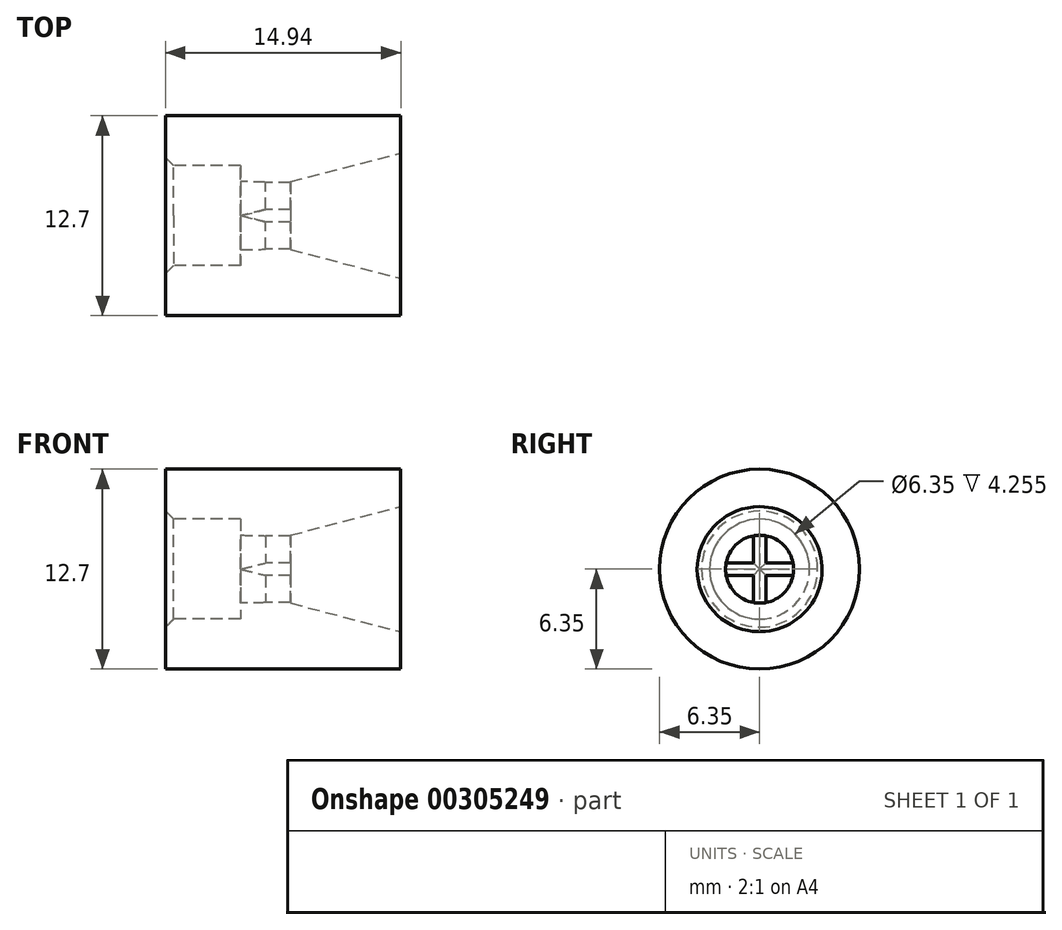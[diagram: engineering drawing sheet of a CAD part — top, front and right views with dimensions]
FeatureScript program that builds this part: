
annotation { "Feature Type Name" : "Feature", "Feature Type Description" : "" }
export const myFeature = defineFeature(function(context is Context, id is Id, definition is map)
    precondition{}
    {
        {
            var Q0;
            Q0=qCreatedBy(makeId("Top.planeOp"),FACE);
            var sketch = newSketch(context, id + "F0", { "sketchPlane" : qUnion([Q0])});
            skLineSegment(sketch, "E0", {"start": v(0, 0) * mm, "end": v(43.8, 0) * mm, "construction": true});
            skLineSegment(sketch, "E1", {"start": v(0, 6.35) * mm, "end": v(0, 3.17) * mm});
            skLineSegment(sketch, "E2", {"start": v(0, 3.17) * mm, "end": v(4.76, 3.17) * mm});
            skLineSegment(sketch, "E3", {"start": v(4.76, 3.17) * mm, "end": v(4.76, 2.16) * mm});
            skLineSegment(sketch, "E4", {"start": v(4.76, 2.16) * mm, "end": v(7.94, 2.16) * mm});
            skLineSegment(sketch, "E5", {"start": v(7.94, 2.16) * mm, "end": v(14.94, 3.97) * mm});
            skLineSegment(sketch, "E6", {"start": v(14.94, 3.97) * mm, "end": v(14.94, 6.35) * mm});
            skLineSegment(sketch, "E7", {"start": v(14.94, 6.35) * mm, "end": v(0, 6.35) * mm});
            skSolve(sketch);
        }
        {
            var Q0;
            Q0 = qSketchRegion(id + "F0", true);
            var Q1;
            Q1=sQuery(id+"F0.wireOp",EDGE,"E0");
            revolve(context, id + "F1", {"entities" : qUnion([Q0]), "axis" : qUnion([Q1]), "revolveType" : RevolveType.FULL});
        }
        {
            var Q0;
            Q0=makeQuery(id+"F1.opRevolve","SWEPT_EDGE",EDGE,{"disambiguationData":[OSD([sQuery(id+"F0.wireOp",EDGE,"E1"),sQuery(id+"F0.wireOp",EDGE,"E2")])]});
            chamfer(context, id + "F2", {"entities" : qUnion([Q0]), "width" : 0.5 * mm, "tangentPropagation" : true});
        }
        {
            var Q0;
            Q0=qCreatedBy(makeId("Top.planeOp"),FACE);
            var sketch = newSketch(context, id + "F3", { "sketchPlane" : qUnion([Q0])});
            skLineSegment(sketch, "E8", {"start": v(4.76, 2.16) * mm, "end": v(7.94, 2.16) * mm});
            skLineSegment(sketch, "E9", {"start": v(7.94, -2.16) * mm, "end": v(4.76, -2.16) * mm});
            skLineSegment(sketch, "E10.0.0", {"start": v(4.76, -3.17) * mm, "end": v(4.76, 3.17) * mm});
            skLineSegment(sketch, "E11.0", {"start": v(7.94, -2.16) * mm, "end": v(7.94, 2.16) * mm});
            skLineSegment(sketch, "E12", {"start": v(4.76, 0) * mm, "end": v(6.35, 0.4) * mm});
            skLineSegment(sketch, "E13", {"start": v(6.35, 0.4) * mm, "end": v(7.94, 0.4) * mm});
            skLineSegment(sketch, "E14", {"start": v(4.76, 0) * mm, "end": v(7.94, 0) * mm, "construction": true});
            skPoint(sketch, "E15", {"position": v(6.35, 0) * mm});
            skLineSegment(sketch, "E16.MirrorCS", {"start": v(6.35, -0.4) * mm, "end": v(7.94, -0.4) * mm});
            skLineSegment(sketch, "E17.MirrorCS", {"start": v(4.76, 0) * mm, "end": v(6.35, -0.4) * mm});
            skSolve(sketch);
        }
        {
            var Q0;
            Q0=makeQuery(id+"F3.imprint","IMPRINT",FACE,{"disambiguationData":[TD([[makeQuery(id+"F3.imprint","IMPRINT",EDGE,{"derivedFrom":sQuery(id+"F3.wireOp",EDGE,"E12")}),-1.0]])]});
            extrude(context, id + "F4", {"entities" : qUnion([Q0]), "depth" : 6.35 * mm, "symmetric" : true});
        }
        {
            var Q0;
            Q0=makeQuery(id+"F4.opExtrude","SWEPT_BODY",BODY,{"disambiguationData":[OSD([sQuery(id+"F3.wireOp",EDGE,"E11.0"),sQuery(id+"F3.wireOp",EDGE,"E12"),sQuery(id+"F3.wireOp",EDGE,"E13"),sQuery(id+"F3.wireOp",EDGE,"E16.MirrorCS"),sQuery(id+"F3.wireOp",EDGE,"E17.MirrorCS")])]});
            var Q1;
            Q1=makeQuery(id+"F1.opRevolve","SWEPT_FACE",FACE,{"disambiguationData":[OSD([sQuery(id+"F0.wireOp",EDGE,"E4")])]});
            circularPattern(context, id + "F5", {"operationType" : NewBodyOperationType.ADD, "entities" : qUnion([Q0]), "axis" : qUnion([Q1]), "angle" : 90 * degree, "instanceCount" : 2, "equalSpace" : true});
        }
    });
